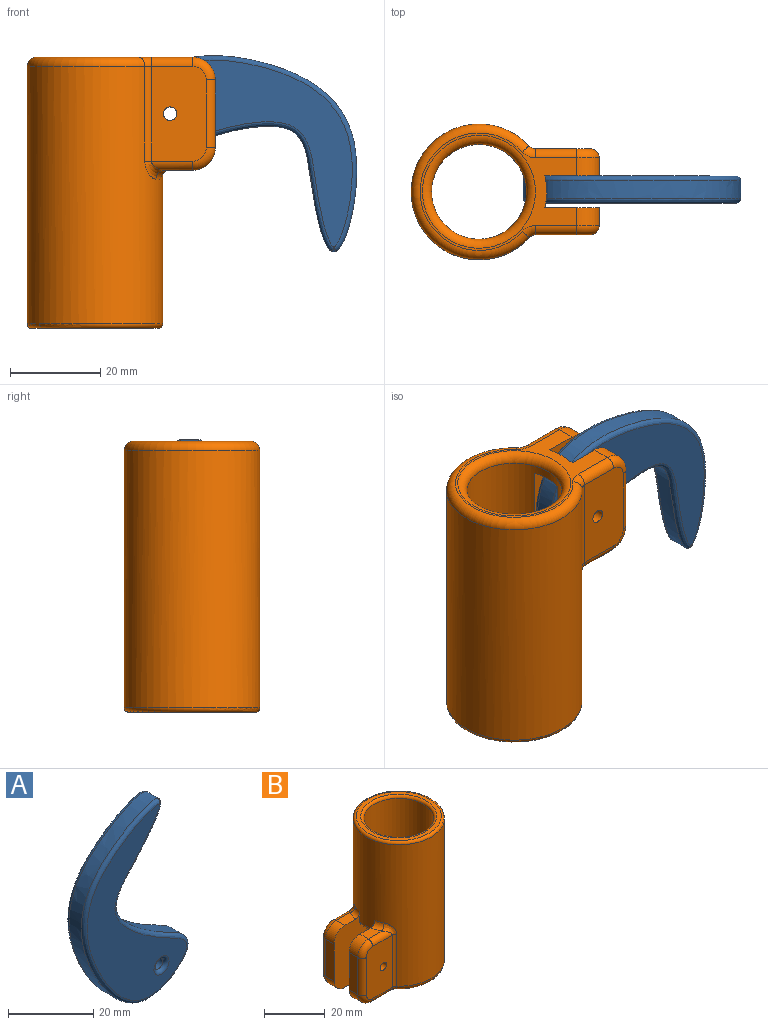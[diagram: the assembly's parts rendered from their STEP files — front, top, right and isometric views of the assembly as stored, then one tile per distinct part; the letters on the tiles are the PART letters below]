
ASSEMBLY  parts=2 mates=1
PART A: 12 faces, bbox 35.1x6x55.8 mm
  f0: extruded ~55.41x34.77mm, area 633.7mm2, adj f6,f7,f8,f9,f10,f11
  f1: plane 53.76x33.07mm, normal (0,-1,0), area 717.2mm2, adj f4,f9,f11
  f2: plane 53.76x33.08mm, normal (0,1,0), area 717.2mm2, adj f5,f6,f8
  f3: cylinder r=1.5mm len=4mm, axis (0,1,0), area 37.7mm2, adj f4,f5
  f4: torus R=2.5mm, axis (0,-1,0), area 18.4mm2, adj f1,f3
  f5: torus R=2.5mm, axis (0,-1,0), area 18.4mm2, adj f2,f3
  f6: bspline ~47.12x24.88mm, area 99.1mm2, adj f0,f2,f7,f8
  f7: bspline ~1x0.98mm, area 0.6mm2, adj f0,f6,f8
  f8: bspline ~55.76x34.96mm, area 146.8mm2, adj f0,f2,f6,f7
  f9: bspline ~46.78x24.88mm, area 98.4mm2, adj f0,f1,f10,f11
  f10: bspline ~1x0.98mm, area 0.6mm2, adj f0,f9,f11
  f11: bspline ~55.76x35.03mm, area 147.5mm2, adj f0,f1,f9,f10
PART B: 46 faces, bbox 43.5x32.7x60.7 mm
  f0: plane 21x12.09mm, normal (0,-1,0), area 242.9mm2, adj f16,f18,f20,f22,f23,f40,f42
  f1: plane 21x12.09mm, normal (0,1,0), area 242.9mm2, adj f17,f25,f27,f29,f30,f36,f38
  f2: cylinder r=10.5mm len=23mm, axis (0,0,-1), area 1396.1mm2, adj f7,f9,f11,f14,f15,f34
  f3: cylinder r=15mm len=57mm, axis (0,0,-1), area 4851mm2, adj f9,f11,f19,f21,f23,f26,f30,f31
  f4: cylinder r=11.5mm len=34mm, axis (0,0,-1), area 2456.7mm2, adj f7,f43
  f5: plane 28x28mm, normal (0,0,1), area 124.9mm2, adj f43,f44
  f6: plane 34.61x26mm, normal (0,0,-1), area 134.3mm2, adj f9,f11,f22,f24,f25,f26,f28,f34
  f7: plane 23x23mm, normal (0,0,1), area 69.1mm2, adj f2,f4
  f8: plane 15x4mm, normal (-1,0,0), area 60mm2, adj f9,f27,f35,f37
  f9: plane 27.25x16.96mm, normal (0,-1,0), area 367.7mm2, adj f2,f3,f6,f8,f10,f14,f15,f17
  f10: plane 6.35x4mm, normal (0,0,1), area 22.3mm2, adj f9,f29,f32,f35
  f11: plane 27.25x16.96mm, normal (0,1,0), area 367.7mm2, adj f2,f3,f6,f12,f13,f14,f15,f16
  f12: plane 15x4mm, normal (-1,0,0), area 60mm2, adj f11,f20,f39,f41
  f13: plane 6.35x4mm, normal (0,0,1), area 22.3mm2, adj f11,f18,f19,f41
  f14: plane 7x3.1mm, normal (0,0,-1), area 17.8mm2, adj f2,f9,f11,f33
  f15: plane 7x1.1mm, normal (0,0,1), area 3.6mm2, adj f2,f9,f11,f45
  f16: cylinder r=1.5mm len=6mm, axis (0,-1,0), area 56.5mm2, adj f0,f11
  f17: cylinder r=1.5mm len=6mm, axis (0,-1,0), area 56.5mm2, adj f1,f9
  f18: cylinder r=2mm len=9.09mm, axis (-1,0,0), area 25.1mm2, adj f0,f13,f21,f42
  f19: torus R=17mm, axis (0,0,1), area 11.6mm2, adj f3,f11,f13,f21
  f20: cylinder r=2mm len=15mm, axis (0,0,-1), area 47.1mm2, adj f0,f12,f40,f42
  f21: bspline ~4.62x4.48mm, area 11.6mm2, adj f3,f18,f19,f23
  f22: cylinder r=2mm len=9.09mm, axis (1,0,0), area 28.6mm2, adj f0,f6,f24,f40
  f23: cylinder r=2mm len=21mm, axis (0,0,-1), area 34.8mm2, adj f0,f3,f21,f24
  f24: torus R=4mm, axis (0,0,1), area 7.1mm2, adj f6,f22,f23,f26
  f25: cylinder r=2mm len=9.09mm, axis (-1,0,0), area 28.6mm2, adj f1,f6,f28,f38
  f26: torus R=13mm, axis (0,0,1), area 215.1mm2, adj f3,f6,f24,f28
  f27: cylinder r=2mm len=15mm, axis (0,0,-1), area 47.1mm2, adj f1,f8,f36,f38
  f28: torus R=4mm, axis (0,0,1), area 7.1mm2, adj f6,f25,f26,f30
  f29: cylinder r=2mm len=9.09mm, axis (1,0,0), area 25.1mm2, adj f1,f10,f31,f36
  f30: cylinder r=2mm len=21mm, axis (0,0,-1), area 34.8mm2, adj f1,f3,f28,f31
  f31: bspline ~4.74x4.45mm, area 11.6mm2, adj f3,f29,f30,f32
  f32: torus R=17mm, axis (0,0,1), area 11.6mm2, adj f3,f9,f10,f31
  f33: torus R=13mm, axis (0,0,1), area 22.7mm2, adj f3,f9,f11,f14
  f34: torus R=12.5mm, axis (0,0,1), area 221.6mm2, adj f2,f6
  f35: cylinder r=5mm len=5mm, axis (0,1,0), area 31.4mm2, adj f8,f9,f10,f36
  f36: torus R=3mm, axis (0,1,0), area 21.1mm2, adj f1,f27,f29,f35
  f37: cylinder r=5mm len=5mm, axis (0,-1,0), area 31.4mm2, adj f6,f8,f9,f38
  f38: torus R=3mm, axis (0,1,0), area 21.1mm2, adj f1,f25,f27,f37
  f39: cylinder r=5mm len=5mm, axis (0,-1,0), area 31.4mm2, adj f6,f11,f12,f40
  f40: torus R=3mm, axis (0,-1,0), area 21.1mm2, adj f0,f20,f22,f39
  f41: cylinder r=5mm len=5mm, axis (0,1,0), area 31.4mm2, adj f11,f12,f13,f42
  f42: torus R=3mm, axis (0,-1,0), area 21.1mm2, adj f0,f18,f20,f41
  f43: torus R=12.5mm, axis (0,0,1), area 117.1mm2, adj f4,f5
  f44: torus R=14mm, axis (0,0,1), area 144.5mm2, adj f3,f5
  f45: torus R=11mm, axis (0,0,1), area 44.5mm2, adj f6,f9,f11,f15
PLACE A rot(axis=(0,1,0),130deg) t=(-15.53,13,8.2)mm
PLACE B rot(axis=(0,1,0),180deg) t=(0,0,59)mm
MATE revolute B.f16 <-> A.f4  axis (0,-1,0) through (16.61,3.5,46.5)mm
